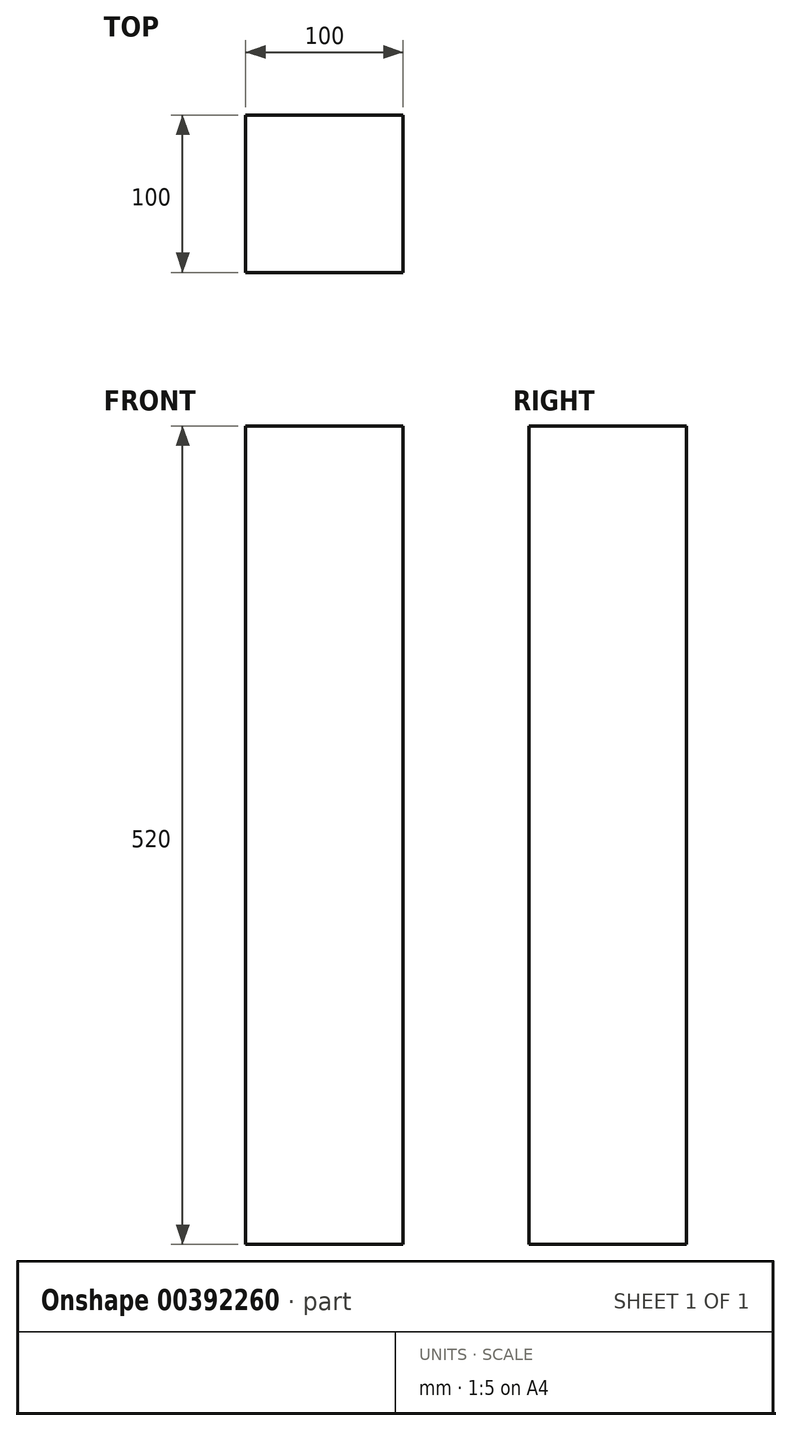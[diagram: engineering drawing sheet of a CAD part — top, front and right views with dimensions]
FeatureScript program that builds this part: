
annotation { "Feature Type Name" : "Feature", "Feature Type Description" : "" }
export const myFeature = defineFeature(function(context is Context, id is Id, definition is map)
    precondition{}
    {
        {
            var Q0;
            Q0=qCreatedBy(makeId("Top.planeOp"),FACE);
            var sketch = newSketch(context, id + "F0", { "sketchPlane" : qUnion([Q0])});
            skLineSegment(sketch, "E0.bottom", {"start": v(50, -50) * mm, "end": v(-50, -50) * mm});
            skLineSegment(sketch, "E0.top", {"start": v(50, 50) * mm, "end": v(-50, 50) * mm});
            skLineSegment(sketch, "E0.left", {"start": v(50, -50) * mm, "end": v(50, 50) * mm});
            skLineSegment(sketch, "E0.right", {"start": v(-50, -50) * mm, "end": v(-50, 50) * mm});
            skPoint(sketch, "E0.middle", {"position": v(0, 0) * mm});
            skSolve(sketch);
        }
        {
            var Q0;
            Q0 = qSketchRegion(id + "F0", true);
            extrude(context, id + "F1", {"entities" : qUnion([Q0]), "depth" : 520 * mm, "offsetDistance" : 25 * mm});
        }
        {
            var Q0;
            Q0=makeQuery(id+"F1.opExtrude","SWEPT_FACE",FACE,{"disambiguationData":[OSD([sQuery(id+"F0.wireOp",EDGE,"E0.left")])]});
            var sketch = newSketch(context, id + "F2", { "sketchPlane" : qUnion([Q0])});
            skLineSegment(sketch, "E1", {"start": v(-50, 0) * mm, "end": v(50, 100) * mm});
            skSolve(sketch);
        }
        {
            var Q0;
            Q0=makeQuery(id+"F1.opExtrude","SWEPT_FACE",FACE,{"disambiguationData":[OSD([sQuery(id+"F0.wireOp",EDGE,"E0.bottom")])]});
            var sketch = newSketch(context, id + "F3", { "sketchPlane" : qUnion([Q0])});
            skLineSegment(sketch, "E2", {"start": v(50, 0) * mm, "end": v(-50, 100) * mm});
            skSolve(sketch);
        }
        {
            var Q0;
            Q0=sQuery(id+"F2.wireOp",EDGE,"E1");
            cPlane(context, id + "F4", {"entities" : qUnion([Q0]), "cplaneType" : CPlaneType.MID_PLANE, "offset" : 25 * mm, "width" : 150 * mm, "height" : 150 * mm});
        }
    });
